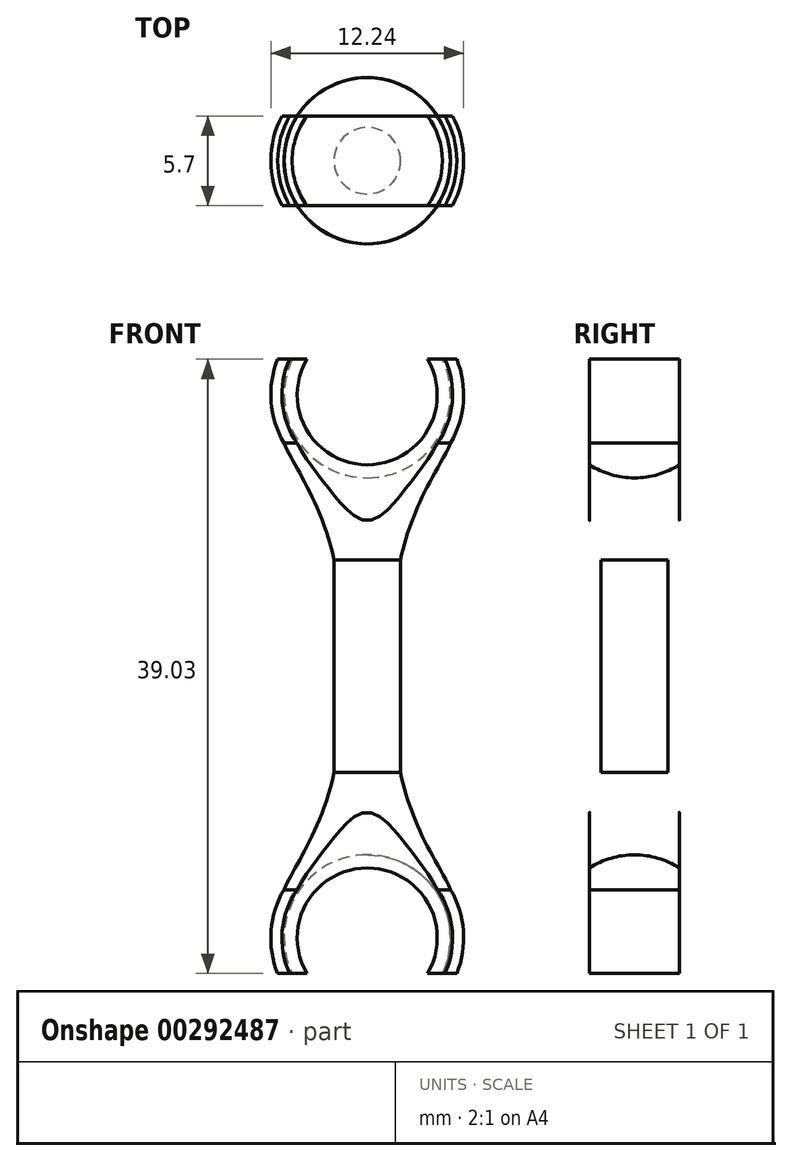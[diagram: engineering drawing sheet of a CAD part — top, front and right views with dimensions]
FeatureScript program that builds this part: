
annotation { "Feature Type Name" : "Feature", "Feature Type Description" : "" }
export const myFeature = defineFeature(function(context is Context, id is Id, definition is map)
    precondition{}
    {
        {
            var Q0;
            Q0=qCreatedBy(makeId("Front.planeOp"),FACE);
            var sketch = newSketch(context, id + "F0", { "sketchPlane" : qUnion([Q0])});
            skLineSegment(sketch, "E0", {"start": v(0, 18.05) * mm, "end": v(0, 5.28) * mm, "construction": true});
            skPoint(sketch, "E0.startSnap0", {"position": v(0, 5.28) * mm});
            skPoint(sketch, "E1.orphan", {"position": v(3.35, 14.95) * mm});
            skLineSegment(sketch, "E2", {"start": v(0, -5) * mm, "end": v(0, 15.08) * mm});
            skLineSegment(sketch, "E3", {"start": v(0, -7.63) * mm, "end": v(0, -5) * mm});
            skLineSegment(sketch, "E4", {"start": v(0, -20.98) * mm, "end": v(0, -7.63) * mm});
            skArc(sketch, "E5", {"start": v(0, -26.2) * mm, "mid": v(-4.46, -28.66) * mm, "end": v(-4.77, -33.75) * mm});
            skLineSegment(sketch, "E6", {"start": v(-5.69, -33.75) * mm, "end": v(-4.77, -33.75) * mm});
            skArc(sketch, "E7.trimOffspring", {"start": v(-5.3, -28.42) * mm, "mid": v(-6.1, -31.04) * mm, "end": v(-5.69, -33.75) * mm});
            skFitSpline(sketch, "E8", {"points": [v(-5.3, -28.42) * mm, v(-2.11, -20.98) * mm], "startDerivative": vector(2.14, 4.77) * mm, "endDerivative": vector(2.36, 11.08) * mm});
            skLineSegment(sketch, "E9", {"start": v(0, -26.2) * mm, "end": v(0, -20.98) * mm});
            skLineSegment(sketch, "E10.trimOffspring", {"start": v(0, 4.53) * mm, "end": v(0, -5) * mm, "construction": true});
            skLineSegment(sketch, "E11", {"start": v(-5.69, -33.75) * mm, "end": v(0, -33.75) * mm, "construction": true});
            skLineSegment(sketch, "E12", {"start": v(0, -33.75) * mm, "end": v(0, 5.28) * mm});
            skLineSegment(sketch, "E13", {"start": v(0, 5.28) * mm, "end": v(1.93, 5.28) * mm, "construction": true});
            skLineSegment(sketch, "E14", {"start": v(0, -33.75) * mm, "end": v(3.11, -33.75) * mm, "construction": true});
            skLineSegment(sketch, "E15", {"start": v(1.93, 5.28) * mm, "end": v(1.93, -33.75) * mm, "construction": true});
            skLineSegment(sketch, "E16", {"start": v(1.93, -14.24) * mm, "end": v(-2.11, -14.24) * mm, "construction": true});
            skLineSegment(sketch, "E17.trimOffspring", {"start": v(-2.11, -14.24) * mm, "end": v(-2.11, -20.98) * mm});
            skPoint(sketch, "E18.end.orphan", {"position": v(0, 10.5) * mm});
            skPoint(sketch, "E19.1.internal.orphan", {"position": v(-2.11, 10.5) * mm});
            skLineSegment(sketch, "E20.MirrorCS", {"start": v(-2.11, -14.24) * mm, "end": v(-2.11, -7.49) * mm});
            skArc(sketch, "E21.MirrorCS", {"start": v(0, -2.26) * mm, "mid": v(-4.46, 0.2) * mm, "end": v(-4.77, 5.28) * mm});
            skFitSpline(sketch, "E22.MirrorCS", {"points": [v(-5.3, -0.05) * mm, v(-2.11, -7.49) * mm], "startDerivative": vector(2.14, -4.77) * mm, "endDerivative": vector(2.36, -11.08) * mm});
            skArc(sketch, "E23.MirrorCS", {"start": v(-5.3, -0.05) * mm, "mid": v(-6.1, 2.57) * mm, "end": v(-5.69, 5.28) * mm});
            skLineSegment(sketch, "E24.MirrorCS", {"start": v(-5.69, 5.28) * mm, "end": v(0, 5.28) * mm, "construction": true});
            skLineSegment(sketch, "E25", {"start": v(-4.77, 5.28) * mm, "end": v(-5.69, 5.28) * mm});
            skSolve(sketch);
        }
        {
            var Q0;
            {var subQ2=sQuery(id+"F0.wireOp",EDGE,"LgFWr4Co-ReSR-DyU5-e4Km-6QeTsJRQIzUY");Q0=makeQuery(id+"F0.imprint","IMPRINT",FACE,{"disambiguationData":[TD([[makeQuery(id+"F0.imprint","IMPRINT",EDGE,{"derivedFrom":subQ2}),1.0]])]});}
            var Q1;
            {var subQ5=sQuery(id+"F0.wireOp",EDGE,"E3");Q1=makeQuery(id+"F0.imprint","IMPRINT",FACE,{"disambiguationData":[TD([[makeQuery(id+"F0.imprint","IMPRINT",EDGE,{"derivedFrom":subQ5}),1.0]])]});}
            var Q2;
            Q2=sQuery(id+"F0.wireOp",EDGE,"E2");
            revolve(context, id + "F1", {"entities" : qUnion([Q0, Q1]), "axis" : qUnion([Q2]), "revolveType" : RevolveType.FULL});
        }
        {
            var Q0;
            {var subQ1=sQuery(id+"F0.wireOp",EDGE,"cWpiQPar-AoDs-ndCC-Nn0c-VqNIVhcjIOBf");Q0=makeQuery(id+"F0.imprint","IMPRINT",FACE,{"disambiguationData":[TD([[makeQuery(id+"F0.imprint","IMPRINT",EDGE,{"derivedFrom":subQ1}),-1.0]])]});}
            var Q1;
            {var subQ11=sQuery(id+"F0.wireOp",EDGE,"E5");Q1=makeQuery(id+"F0.imprint","IMPRINT",FACE,{"disambiguationData":[TD([[makeQuery(id+"F0.imprint","IMPRINT",EDGE,{"derivedFrom":subQ11}),-1.0]])]});}
            var Q2;
            Q2=sQuery(id+"F0.wireOp",EDGE,"E2");
            revolve(context, id + "F2", {"entities" : qUnion([Q0, Q1]), "axis" : qUnion([Q2]), "revolveType" : RevolveType.FULL});
        }
        {
            var Q0;
            Q0=qCreatedBy(makeId("Top.planeOp"),FACE);
            var sketch = newSketch(context, id + "F3", { "sketchPlane" : qUnion([Q0])});
            skLineSegment(sketch, "E26", {"start": v(0, 0) * mm, "end": v(0, -2.85) * mm, "construction": true});
            skLineSegment(sketch, "E27", {"start": v(0, -2.85) * mm, "end": v(7.27, -2.85) * mm});
            skLineSegment(sketch, "E28", {"start": v(7.27, -2.85) * mm, "end": v(7.27, -6.57) * mm});
            skLineSegment(sketch, "E29", {"start": v(7.27, -6.57) * mm, "end": v(0, -6.57) * mm});
            skLineSegment(sketch, "E30", {"start": v(9.37, 0) * mm, "end": v(-12.04, 0) * mm, "construction": true});
            skLineSegment(sketch, "E31.MirrorCS", {"start": v(-7.27, -6.57) * mm, "end": v(0, -6.57) * mm});
            skLineSegment(sketch, "E32.MirrorCS", {"start": v(-7.27, -2.85) * mm, "end": v(-7.27, -6.57) * mm});
            skLineSegment(sketch, "E33.MirrorCS", {"start": v(0, -2.85) * mm, "end": v(-7.27, -2.85) * mm});
            skLineSegment(sketch, "E34.MirrorCS", {"start": v(0, 2.85) * mm, "end": v(7.27, 2.85) * mm});
            skLineSegment(sketch, "E35.MirrorCS", {"start": v(0, 2.85) * mm, "end": v(-7.27, 2.85) * mm});
            skLineSegment(sketch, "E36.MirrorCS", {"start": v(-7.27, 2.85) * mm, "end": v(-7.27, 6.57) * mm});
            skLineSegment(sketch, "E37.MirrorCS", {"start": v(-7.27, 6.57) * mm, "end": v(0, 6.57) * mm});
            skLineSegment(sketch, "E38.MirrorCS", {"start": v(7.27, 6.57) * mm, "end": v(0, 6.57) * mm});
            skLineSegment(sketch, "E39.MirrorCS", {"start": v(7.27, 2.85) * mm, "end": v(7.27, 6.57) * mm});
            skSolve(sketch);
        }
        {
            var Q0;
            Q0=makeQuery(id+"F3.imprint","IMPRINT",FACE,{"disambiguationData":[TD([[makeQuery(id+"F3.imprint","IMPRINT",EDGE,{"derivedFrom":sQuery(id+"F3.wireOp",EDGE,"E27")}),-1.0]])]});
            var Q1;
            Q1=makeQuery(id+"F3.imprint","IMPRINT",FACE,{"disambiguationData":[TD([[makeQuery(id+"F3.imprint","IMPRINT",EDGE,{"derivedFrom":sQuery(id+"F3.wireOp",EDGE,"E34.MirrorCS")}),1.0]])]});
            extrude(context, id + "F4", {"entities" : qUnion([Q0, Q1]), "operationType" : NewBodyOperationType.REMOVE, "oppositeDirection" : true, "depth" : 45.8 * mm, "hasSecondDirection" : true, "secondDirectionOppositeDirection" : false, "secondDirectionDepth" : 25 * mm});
        }
        {
            var Q0;
            Q0=makeQuery(id+"F3.imprint","IMPRINT",FACE,{"disambiguationData":[TD([[makeQuery(id+"F3.imprint","IMPRINT",EDGE,{"derivedFrom":sQuery(id+"F3.wireOp",EDGE,"E34.MirrorCS")}),1.0]])]});
            var Q1;
            Q1=makeQuery(id+"F3.imprint","IMPRINT",FACE,{"disambiguationData":[TD([[makeQuery(id+"F3.imprint","IMPRINT",EDGE,{"derivedFrom":sQuery(id+"F3.wireOp",EDGE,"E27")}),-1.0]])]});
            extrude(context, id + "F5", {"entities" : qUnion([Q0, Q1]), "operationType" : NewBodyOperationType.REMOVE, "oppositeDirection" : true, "depth" : 38.4 * mm, "hasSecondDirection" : true, "secondDirectionOppositeDirection" : true, "secondDirectionDepth" : 18.8 * mm});
        }
    });
